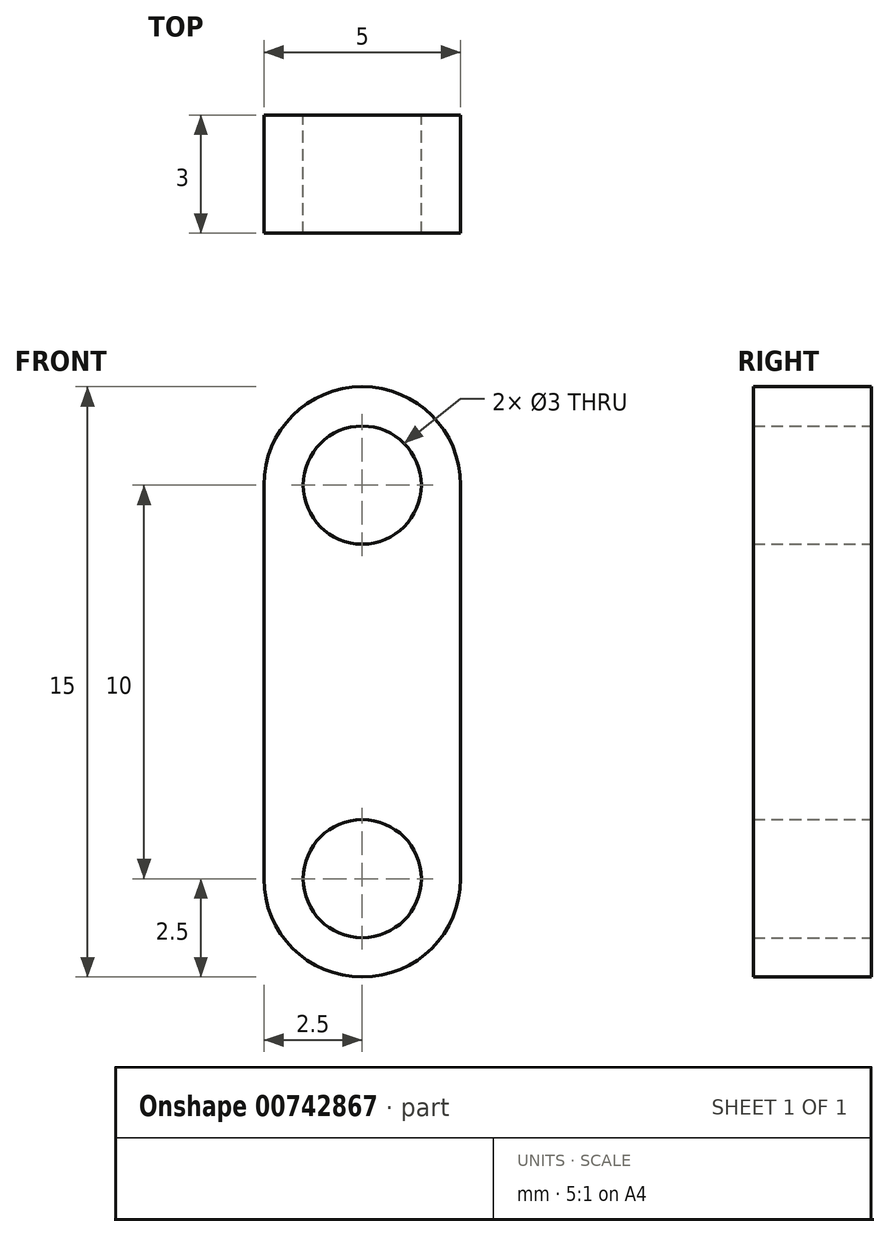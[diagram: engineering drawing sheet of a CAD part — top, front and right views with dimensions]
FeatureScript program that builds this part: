
annotation { "Feature Type Name" : "Feature", "Feature Type Description" : "" }
export const myFeature = defineFeature(function(context is Context, id is Id, definition is map)
    precondition{}
    {
        {
            var Q0;
            Q0=qCreatedBy(makeId("Front.planeOp"),FACE);
            var sketch = newSketch(context, id + "F0", { "sketchPlane" : qUnion([Q0])});
            skLineSegment(sketch, "E0.bottom", {"start": v(2.5, 5) * mm, "end": v(-2.5, 5) * mm, "construction": true});
            skLineSegment(sketch, "E0.top", {"start": v(2.5, -5) * mm, "end": v(-2.5, -5) * mm, "construction": true});
            skLineSegment(sketch, "E0.left", {"start": v(2.5, 5) * mm, "end": v(2.5, -5) * mm});
            skLineSegment(sketch, "E0.right", {"start": v(-2.5, 5) * mm, "end": v(-2.5, -5) * mm});
            skPoint(sketch, "E0.middle", {"position": v(0, 0) * mm});
            skArc(sketch, "E1", {"start": v(2.5, 5) * mm, "mid": v(0, 7.5) * mm, "end": v(-2.5, 5) * mm});
            skArc(sketch, "E2", {"start": v(-2.5, -5) * mm, "mid": v(0, -7.5) * mm, "end": v(2.5, -5) * mm});
            skCircle(sketch, "E3", {"center": v(0, 5) * mm, "radius": 1.5 * mm});
            skCircle(sketch, "E4", {"center": v(0, -5) * mm, "radius": 1.5 * mm});
            skSolve(sketch);
        }
        {
            var Q0;
            Q0 = qSketchRegion(id + "F0", true);
            extrude(context, id + "F1", {"entities" : qUnion([Q0]), "depth" : 3 * mm, "offsetDistance" : 25 * mm});
        }
    });
